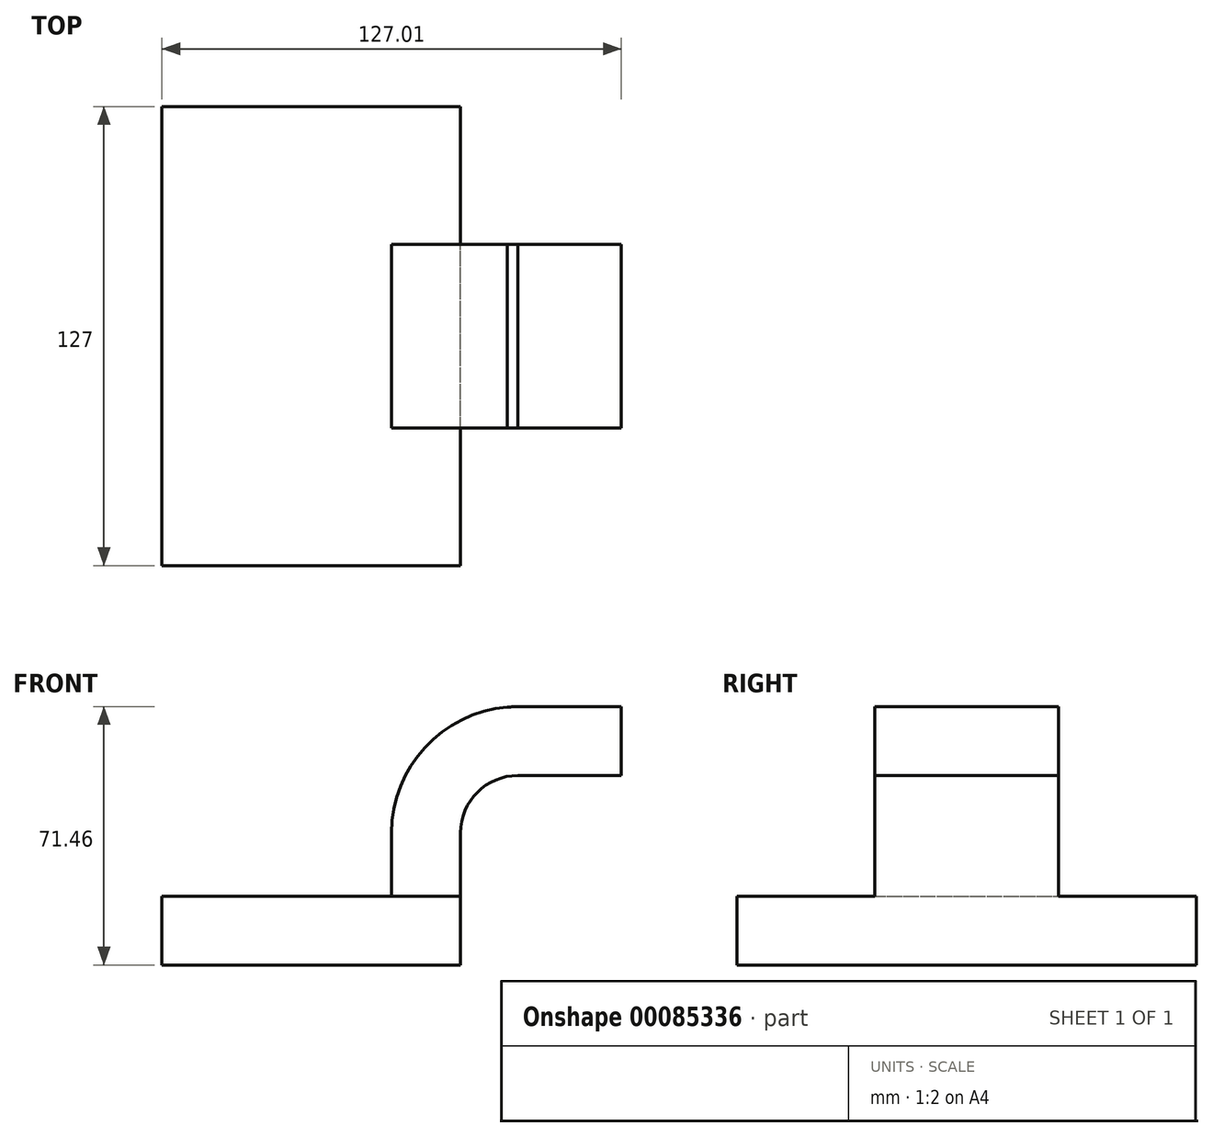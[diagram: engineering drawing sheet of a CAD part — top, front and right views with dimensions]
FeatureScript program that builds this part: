
annotation { "Feature Type Name" : "Feature", "Feature Type Description" : "" }
export const myFeature = defineFeature(function(context is Context, id is Id, definition is map)
    precondition{}
    {
        {
            var Q0;
            Q0=qCreatedBy(makeId("Front.planeOp"),FACE);
            var sketch = newSketch(context, id + "F0", { "sketchPlane" : qUnion([Q0])});
            skLineSegment(sketch, "E0.bottom", {"start": v(-41.28, -9.53) * mm, "end": v(41.28, -9.53) * mm});
            skLineSegment(sketch, "E0.top", {"start": v(-41.28, 9.53) * mm, "end": v(41.28, 9.53) * mm});
            skLineSegment(sketch, "E0.left", {"start": v(-41.28, -9.53) * mm, "end": v(-41.28, 9.53) * mm});
            skLineSegment(sketch, "E0.right", {"start": v(41.28, -9.53) * mm, "end": v(41.28, 9.53) * mm});
            skPoint(sketch, "E0.middle", {"position": v(0, 0) * mm});
            skLineSegment(sketch, "E1.bottom", {"start": v(60.32, 38.1) * mm, "end": v(111.12, 38.1) * mm});
            skLineSegment(sketch, "E1.top", {"start": v(60.32, 66.67) * mm, "end": v(111.12, 66.67) * mm});
            skLineSegment(sketch, "E1.left", {"start": v(60.32, 38.1) * mm, "end": v(60.32, 66.67) * mm});
            skLineSegment(sketch, "E1.right", {"start": v(111.12, 38.1) * mm, "end": v(111.12, 66.67) * mm});
            skPoint(sketch, "E1.middle", {"position": v(85.72, 52.39) * mm});
            skLineSegment(sketch, "E2", {"start": v(41.28, 9.53) * mm, "end": v(41.28, 27) * mm});
            skArc(sketch, "E3", {"start": v(41.27, 27) * mm, "mid": v(45.92, 38.23) * mm, "end": v(57.15, 42.88) * mm});
            skLineSegment(sketch, "E4", {"start": v(57.15, 42.88) * mm, "end": v(85.72, 42.88) * mm});
            skPoint(sketch, "E4.endSnap0", {"position": v(85.72, 38.1) * mm});
            skLineSegment(sketch, "E5.0", {"start": v(57.15, 61.93) * mm, "end": v(85.72, 61.93) * mm});
            skArc(sketch, "E5.1", {"start": v(22.23, 27) * mm, "mid": v(32.45, 51.7) * mm, "end": v(57.15, 61.93) * mm});
            skLineSegment(sketch, "E5.2", {"start": v(22.22, 9.53) * mm, "end": v(22.22, 27) * mm});
            skLineSegment(sketch, "E6", {"start": v(85.72, 38.1) * mm, "end": v(85.72, 66.67) * mm});
            skFitSpline(sketch, "E7", {"points": [v(-41.28, 9.52) * mm, v(57.15, 61.93) * mm], "startDerivative": vector(1.36, 73.04) * mm, "endDerivative": vector(126.6, 3.56) * mm});
            skSolve(sketch);
        }
        {
            var Q0;
            Q0=makeQuery(id+"F0.imprint","IMPRINT",FACE,{"disambiguationData":[TD([[makeQuery(id+"F0.imprint","IMPRINT",EDGE,{"derivedFrom":sQuery(id+"F0.wireOp",EDGE,"E0.bottom")}),1.0]])]});
            extrude(context, id + "F1", {"entities" : qUnion([Q0]), "endBound" : BoundingType.SYMMETRIC, "depth" : 127 * mm});
        }
        {
            var Q0;
            {var subQ1=sQuery(id+"F0.wireOp",EDGE,"E2");Q0=makeQuery(id+"F0.imprint","IMPRINT",FACE,{"disambiguationData":[TD([[makeQuery(id+"F0.imprint","IMPRINT",EDGE,{"derivedFrom":subQ1}),1.0]])]});}
            var Q1;
            {var subQ0=sQuery(id+"F0.wireOp",EDGE,"E4");var subQ1=sQuery(id+"F0.wireOp",EDGE,"E1.left");var subQ2=makeQuery(id+"F0.imprint","INTERSECT",VERTEX,{"derivedFrom":[subQ1,subQ0]});Q1=makeQuery(id+"F0.imprint","IMPRINT",FACE,{"disambiguationData":[TD([[makeQuery(id+"F0.imprint","IMPRINT",EDGE,{"disambiguationData":[TD([[subQ2,-1.0]])],"derivedFrom":subQ1}),-1.0]])]});}
            extrude(context, id + "F2", {"entities" : qUnion([Q0, Q1]), "operationType" : NewBodyOperationType.ADD, "endBound" : BoundingType.SYMMETRIC, "depth" : 50.8 * mm});
        }
    });
